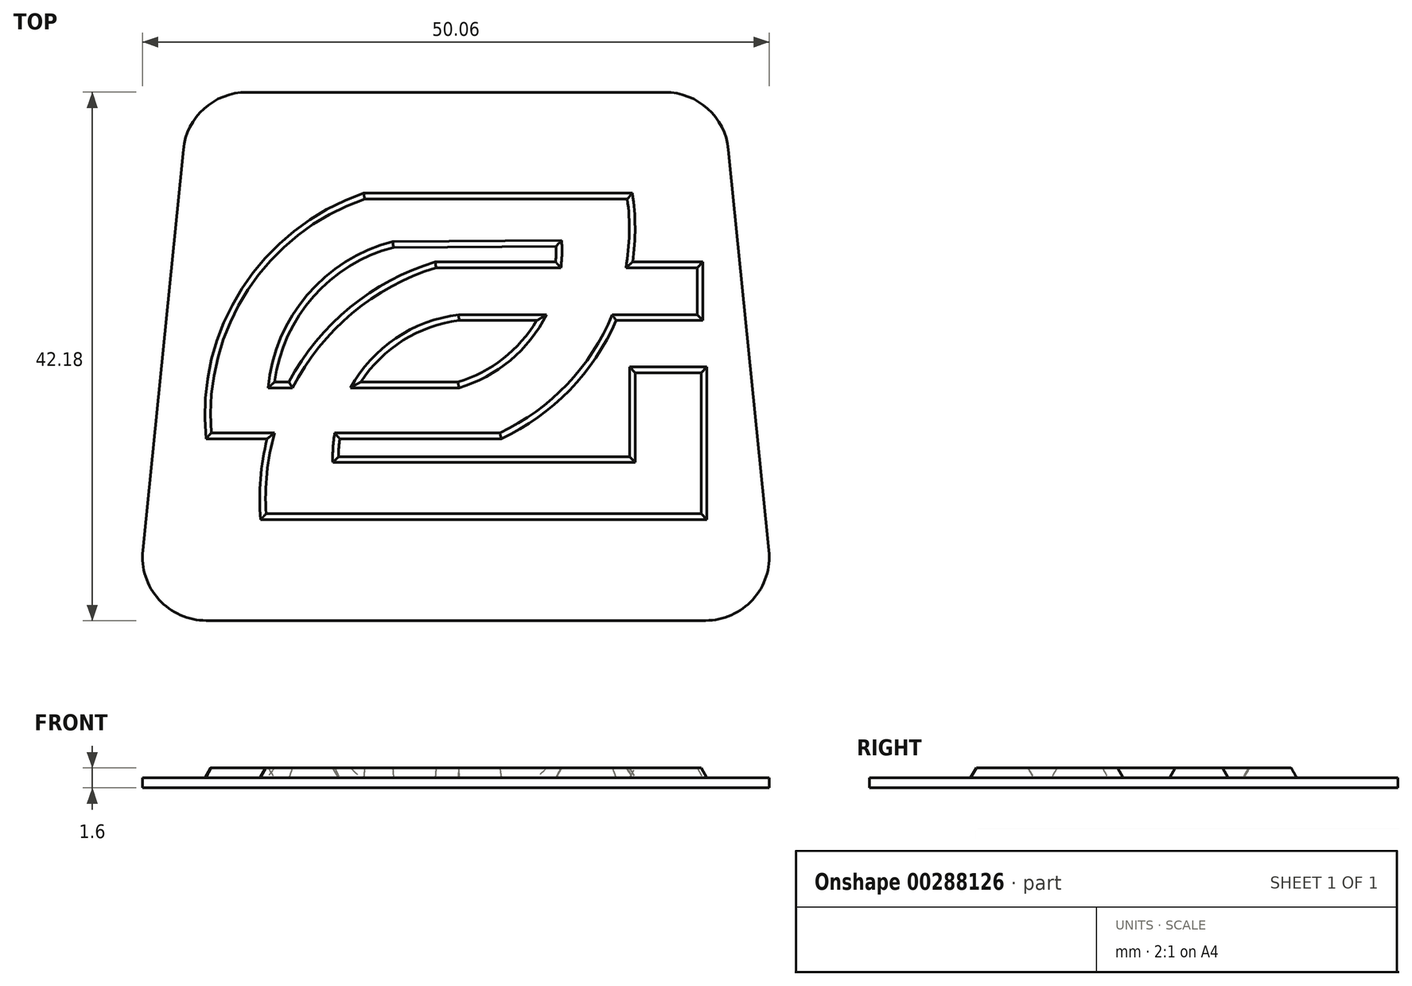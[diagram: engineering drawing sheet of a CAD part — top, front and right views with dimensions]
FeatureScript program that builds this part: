
annotation { "Feature Type Name" : "Feature", "Feature Type Description" : "" }
export const myFeature = defineFeature(function(context is Context, id is Id, definition is map)
    precondition{}
    {
        {
            var Q0;
            Q0=qCreatedBy(makeId("Top.planeOp"),FACE);
            var sketch = newSketch(context, id + "F0", { "sketchPlane" : qUnion([Q0])});
            skLineSegment(sketch, "E0", {"start": v(-26.97, -22.35) * mm, "end": v(26.97, -22.35) * mm});
            skLineSegment(sketch, "E1", {"start": v(26.97, -22.35) * mm, "end": v(22.45, 22.35) * mm});
            skLineSegment(sketch, "E2", {"start": v(22.45, 22.35) * mm, "end": v(-2.7, 22.35) * mm});
            skLineSegment(sketch, "E3", {"start": v(-2.7, 22.35) * mm, "end": v(-22.45, 22.35) * mm});
            skLineSegment(sketch, "E4", {"start": v(-22.45, 22.35) * mm, "end": v(-26.97, -22.35) * mm});
            skLineSegment(sketch, "E5", {"start": v(16.7, 21.09) * mm, "end": v(-2, 21.09) * mm});
            skLineSegment(sketch, "E6", {"start": v(-2, 21.09) * mm, "end": v(-16.7, 21.09) * mm});
            skLineSegment(sketch, "E7", {"start": v(25, -15.48) * mm, "end": v(21.76, 16.5) * mm});
            skLineSegment(sketch, "E8", {"start": v(-19.93, -21.09) * mm, "end": v(19.93, -21.09) * mm});
            skLineSegment(sketch, "E9", {"start": v(-21.76, 16.5) * mm, "end": v(-25, -15.48) * mm});
            skArc(sketch, "E10", {"start": v(-16.7, 21.09) * mm, "mid": v(-20.11, 19.77) * mm, "end": v(-21.76, 16.5) * mm});
            skArc(sketch, "E11", {"start": v(21.76, 16.5) * mm, "mid": v(20.11, 19.77) * mm, "end": v(16.7, 21.09) * mm});
            skArc(sketch, "E12", {"start": v(19.93, -21.09) * mm, "mid": v(23.71, -19.4) * mm, "end": v(25, -15.48) * mm});
            skArc(sketch, "E13", {"start": v(-25, -15.48) * mm, "mid": v(-23.71, -19.4) * mm, "end": v(-19.93, -21.09) * mm});
            skSolve(sketch);
        }
        {
            var Q0;
            Q0=makeQuery(id+"F0.imprint","IMPRINT",FACE,{"disambiguationData":[TD([[makeQuery(id+"F0.imprint","IMPRINT",EDGE,{"derivedFrom":sQuery(id+"F0.wireOp",EDGE,"E5")}),1.0]])]});
            extrude(context, id + "F1", {"entities" : qUnion([Q0]), "depth" : .8 * mm});
        }
        {
            var Q0;
            Q0=makeQuery(id+"F1.opExtrude","CAP_FACE",FACE,{"disambiguationData":[OSD([sQuery(id+"F0.wireOp",EDGE,"E5"),sQuery(id+"F0.wireOp",EDGE,"E6"),sQuery(id+"F0.wireOp",EDGE,"E7"),sQuery(id+"F0.wireOp",EDGE,"E8"),sQuery(id+"F0.wireOp",EDGE,"E9"),sQuery(id+"F0.wireOp",EDGE,"E10"),sQuery(id+"F0.wireOp",EDGE,"E11"),sQuery(id+"F0.wireOp",EDGE,"E12"),sQuery(id+"F0.wireOp",EDGE,"E13")])],"isStart":false});
            var sketch = newSketch(context, id + "F2", { "sketchPlane" : qUnion([Q0])});
            skLineSegment(sketch, "E14", {"start": v(13.86, -0.84) * mm, "end": v(20.05, -0.84) * mm});
            skLineSegment(sketch, "E15", {"start": v(20.05, -0.84) * mm, "end": v(20.05, -13.03) * mm});
            skLineSegment(sketch, "E16", {"start": v(20.05, -13.03) * mm, "end": v(-15.59, -13.03) * mm});
            skLineSegment(sketch, "E17", {"start": v(13.86, -0.84) * mm, "end": v(13.86, -8) * mm});
            skLineSegment(sketch, "E18", {"start": v(13.86, -8) * mm, "end": v(-9.37, -8) * mm});
            skArc(sketch, "E19", {"start": v(0.25, 2.86) * mm, "mid": v(-6.61, -0.76) * mm, "end": v(-9.37, -8) * mm});
            skLineSegment(sketch, "E20", {"start": v(0.25, 2.86) * mm, "end": v(6.46, 2.86) * mm});
            skLineSegment(sketch, "E21", {"start": v(12.8, 2.86) * mm, "end": v(19.72, 2.86) * mm});
            skLineSegment(sketch, "E22", {"start": v(19.72, 2.86) * mm, "end": v(19.72, 7.54) * mm});
            skLineSegment(sketch, "E23", {"start": v(19.72, 7.54) * mm, "end": v(13.86, 7.54) * mm});
            skLineSegment(sketch, "E24", {"start": v(7.97, 7.54) * mm, "end": v(-1.65, 7.54) * mm});
            skArc(sketch, "E25", {"start": v(-1.65, 7.54) * mm, "mid": v(-12.26, -0.28) * mm, "end": v(-15.59, -13.03) * mm});
            skArc(sketch, "E26", {"start": v(-7.36, 13.03) * mm, "mid": v(-17.08, 5.42) * mm, "end": v(-19.95, -6.57) * mm});
            skLineSegment(sketch, "E27", {"start": v(-7.36, 13.03) * mm, "end": v(14.1, 13.03) * mm});
            skArc(sketch, "E28", {"start": v(3.62, -6.57) * mm, "mid": v(12.13, 1.48) * mm, "end": v(14.1, 13.03) * mm});
            skLineSegment(sketch, "E29", {"start": v(3.62, -6.57) * mm, "end": v(-9.27, -6.57) * mm});
            skLineSegment(sketch, "E30", {"start": v(-15.07, -6.57) * mm, "end": v(-19.95, -6.57) * mm});
            skArc(sketch, "E31", {"start": v(-4.98, 8.7) * mm, "mid": v(-11.37, 4.78) * mm, "end": v(-14.47, -2.05) * mm});
            skLineSegment(sketch, "E32", {"start": v(-4.98, 8.7) * mm, "end": v(8, 8.8) * mm});
            skArc(sketch, "E33", {"start": v(0.17, -2.05) * mm, "mid": v(5.92, 2.05) * mm, "end": v(8, 8.8) * mm});
            skLineSegment(sketch, "E34", {"start": v(0.17, -2.05) * mm, "end": v(-7.6, -2.05) * mm});
            skLineSegment(sketch, "E35", {"start": v(-13.33, -2.05) * mm, "end": v(-14.47, -2.05) * mm});
            skSolve(sketch);
        }
        {
            var Q0;
            Q0=makeQuery(id+"F2.imprint","IMPRINT",FACE,{"disambiguationData":[TD([[makeQuery(id+"F2.imprint","IMPRINT",EDGE,{"derivedFrom":sQuery(id+"F2.wireOp",EDGE,"E26")}),1.0]])]});
            var Q1;
            Q1=makeQuery(id+"F2.imprint","IMPRINT",FACE,{"disambiguationData":[TD([[makeQuery(id+"F2.imprint","IMPRINT",EDGE,{"derivedFrom":sQuery(id+"F2.wireOp",EDGE,"E14")}),-1.0]])]});
            var Q2;
            {var subQ0=sQuery(id+"F2.wireOp",EDGE,"E21");Q2=makeQuery(id+"F2.imprint","IMPRINT",FACE,{"disambiguationData":[TD([[makeQuery(id+"F2.imprint","IMPRINT",EDGE,{"derivedFrom":subQ0}),1.0]])]});}
            extrude(context, id + "F3", {"entities" : qUnion([Q0, Q1, Q2]), "depth" : .8 * mm, "hasDraft" : true, "draftAngle" : 30 * degree, "draftPullDirection" : true});
        }
    });
